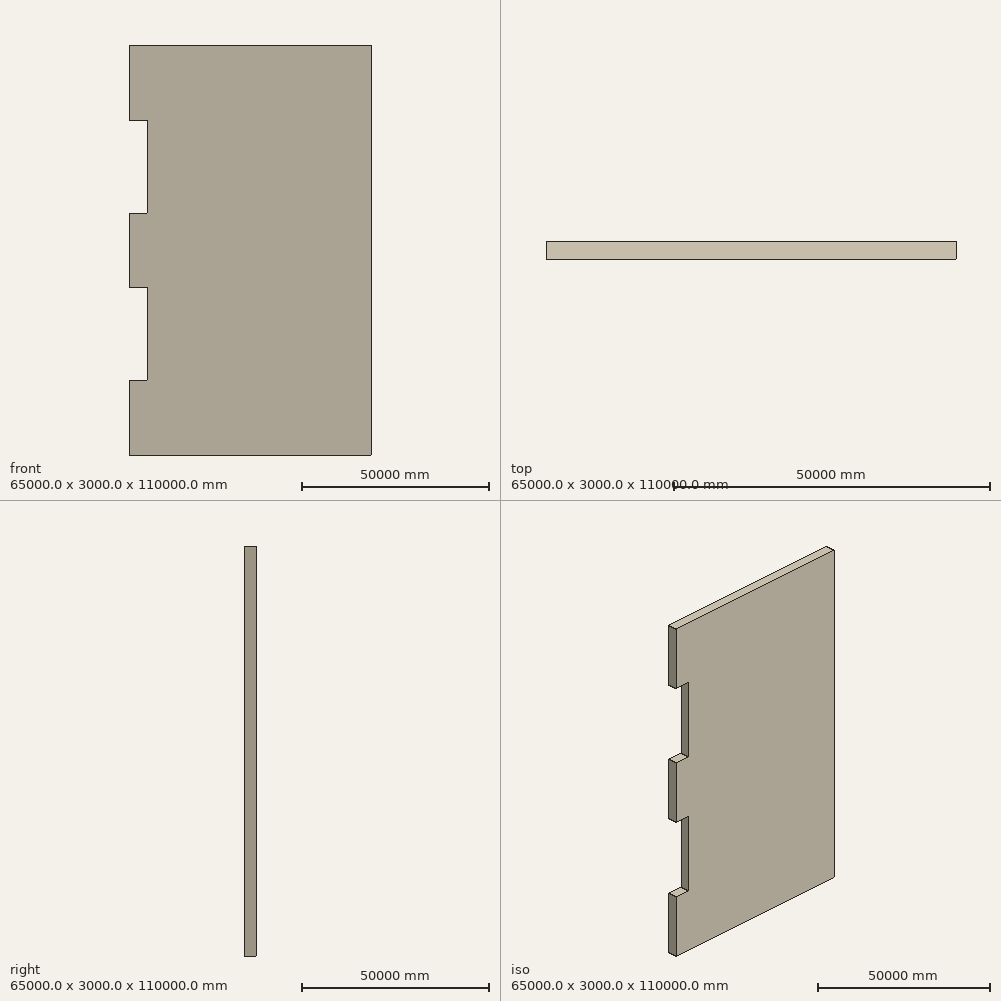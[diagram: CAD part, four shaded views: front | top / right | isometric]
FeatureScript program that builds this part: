
annotation { "Feature Type Name" : "Feature", "Feature Type Description" : "" }
export const myFeature = defineFeature(function(context is Context, id is Id, definition is map)
    precondition{}
    {
        {
            var Q0;
            Q0=qCreatedBy(makeId("Front.planeOp"),FACE);
            var sketch = newSketch(context, id + "F0", { "sketchPlane" : qUnion([Q0])});
            skLineSegment(sketch, "E0.bottom", {"start": v(-30000, 55000) * mm, "end": v(30000, 55000) * mm});
            skLineSegment(sketch, "E0.top", {"start": v(-30000, -55000) * mm, "end": v(30000, -55000) * mm});
            skLineSegment(sketch, "E0.left", {"start": v(-30000, 55000) * mm, "end": v(-30000, -55000) * mm});
            skLineSegment(sketch, "E0.right", {"start": v(30000, 55000) * mm, "end": v(30000, -55000) * mm});
            skPoint(sketch, "E0.middle", {"position": v(0, 0) * mm});
            skLineSegment(sketch, "E1.bottom", {"start": v(-35000, 55000) * mm, "end": v(-30000, 55000) * mm});
            skLineSegment(sketch, "E1.top", {"start": v(-35000, 35000) * mm, "end": v(-30000, 35000) * mm});
            skLineSegment(sketch, "E1.left", {"start": v(-35000, 55000) * mm, "end": v(-35000, 35000) * mm});
            skLineSegment(sketch, "E1.right", {"start": v(-30000, 55000) * mm, "end": v(-30000, 35000) * mm});
            skLineSegment(sketch, "E2.bottom", {"start": v(-35000, 10000) * mm, "end": v(-30000, 10000) * mm});
            skLineSegment(sketch, "E2.top", {"start": v(-35000, -10000) * mm, "end": v(-30000, -10000) * mm});
            skLineSegment(sketch, "E2.left", {"start": v(-35000, 10000) * mm, "end": v(-35000, -10000) * mm});
            skLineSegment(sketch, "E2.right", {"start": v(-30000, 10000) * mm, "end": v(-30000, -10000) * mm});
            skLineSegment(sketch, "E3.bottom", {"start": v(-35000, -35000) * mm, "end": v(-30000, -35000) * mm});
            skLineSegment(sketch, "E3.top", {"start": v(-35000, -55000) * mm, "end": v(-30000, -55000) * mm});
            skLineSegment(sketch, "E3.left", {"start": v(-35000, -35000) * mm, "end": v(-35000, -55000) * mm});
            skLineSegment(sketch, "E3.right", {"start": v(-30000, -35000) * mm, "end": v(-30000, -55000) * mm});
            skSolve(sketch);
        }
        {
            var Q0;
            Q0 = qSketchRegion(id + "F0", true);
            extrude(context, id + "F1", {"entities" : qUnion([Q0]), "endBound" : BoundingType.SYMMETRIC, "depth" : 3000 * mm, "offsetDistance" : 25 * mm});
        }
    });
